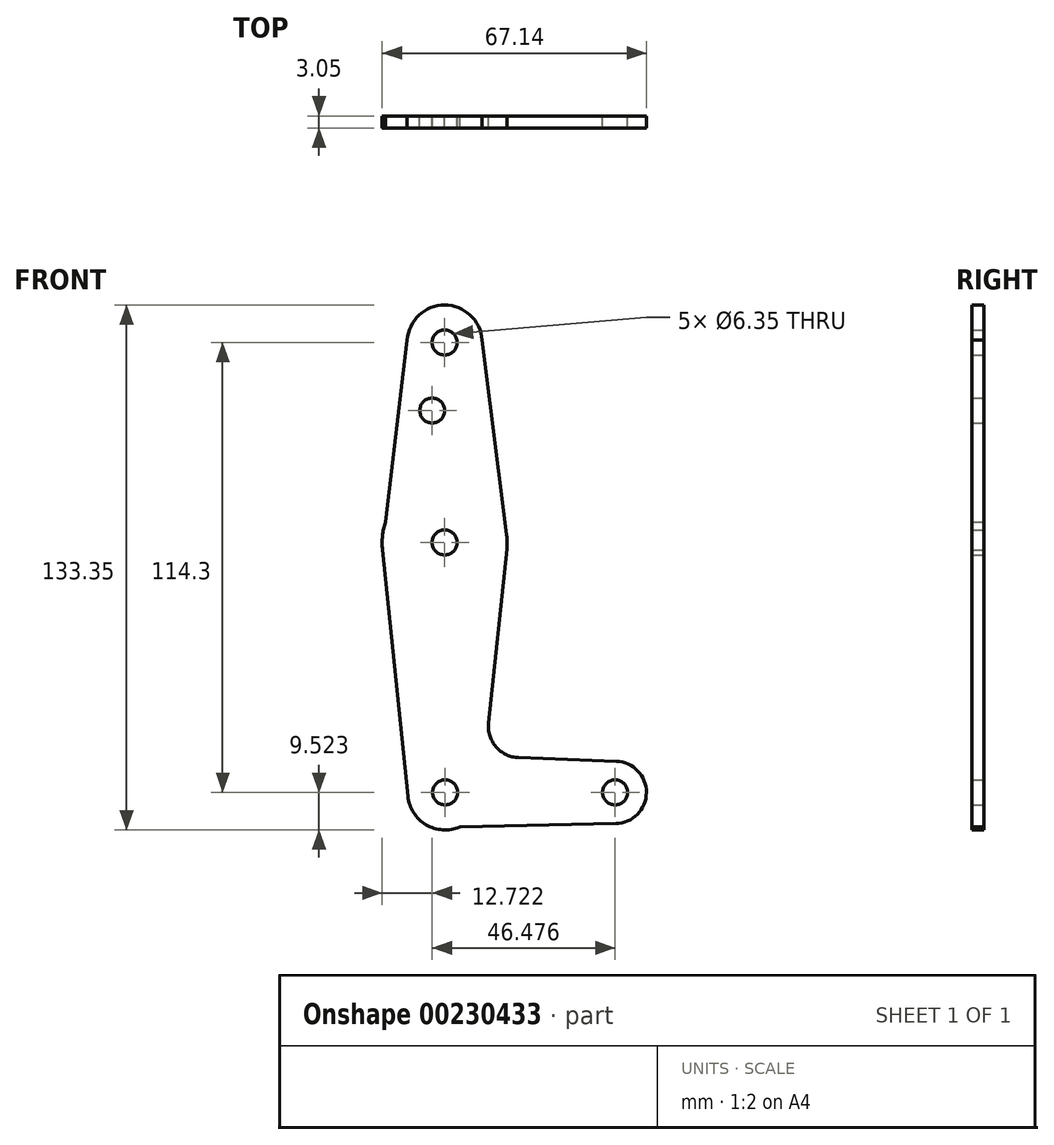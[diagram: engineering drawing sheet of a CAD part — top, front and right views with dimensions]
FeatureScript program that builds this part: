
annotation { "Feature Type Name" : "Feature", "Feature Type Description" : "" }
export const myFeature = defineFeature(function(context is Context, id is Id, definition is map)
    precondition{}
    {
        {
            var Q0;
            Q0=qCreatedBy(makeId("Front.planeOp"),FACE);
            var sketch = newSketch(context, id + "F0", { "sketchPlane" : qUnion([Q0])});
            skLineSegment(sketch, "E0", {"start": v(-35.23, -15.74) * mm, "end": v(7.95, -15.74) * mm});
            skCircle(sketch, "E1", {"center": v(-35.37, 98.56) * mm, "radius": 9.53 * mm});
            skCircle(sketch, "E2", {"center": v(-35.37, 47.76) * mm, "radius": 15.88 * mm});
            skCircle(sketch, "E3", {"center": v(-35.23, -15.74) * mm, "radius": 9.53 * mm});
            skCircle(sketch, "E4", {"center": v(7.95, -15.74) * mm, "radius": 7.94 * mm});
            skLineSegment(sketch, "E5", {"start": v(-35.37, 98.56) * mm, "end": v(-35.23, -15.74) * mm});
            skLineSegment(sketch, "E6", {"start": v(-44.88, 99.17) * mm, "end": v(-50.4, 52.9) * mm});
            skLineSegment(sketch, "E7", {"start": v(-25.87, 99.2) * mm, "end": v(-19.62, 49.75) * mm});
            skLineSegment(sketch, "E8", {"start": v(-19.59, 46.1) * mm, "end": v(-24.22, 1.88) * mm});
            skLineSegment(sketch, "E9", {"start": v(-51.2, 46.42) * mm, "end": v(-44.7, -16.71) * mm});
            skLineSegment(sketch, "E10", {"start": v(-38.57, -24.66) * mm, "end": v(8.12, -23.67) * mm});
            skLineSegment(sketch, "E11", {"start": v(-16.6, -6.9) * mm, "end": v(8.24, -7.8) * mm});
            skCircle(sketch, "E12", {"center": v(-35.37, 98.56) * mm, "radius": 3.18 * mm});
            skCircle(sketch, "E13", {"center": v(-38.53, 81.29) * mm, "radius": 3.18 * mm});
            skCircle(sketch, "E14", {"center": v(-35.37, 47.76) * mm, "radius": 3.18 * mm});
            skCircle(sketch, "E15", {"center": v(-35.23, -15.74) * mm, "radius": 3.18 * mm});
            skCircle(sketch, "E16", {"center": v(7.95, -15.74) * mm, "radius": 3.18 * mm});
            skArc(sketch, "E17.filletArc", {"start": v(-24.22, 1.88) * mm, "mid": v(-22.32, -4.16) * mm, "end": v(-16.6, -6.9) * mm});
            skSolve(sketch);
        }
        {
            var Q0;
            Q0 = qSketchRegion(id + "F0", true);
            extrude(context, id + "F1", {"entities" : qUnion([Q0]), "depth" : 3.05 * mm});
        }
        {
            var Q0;
            {var subQ0=sQuery(id+"F0.wireOp",EDGE,"E15");var subQ1=sQuery(id+"F0.wireOp",EDGE,"E0");var subQ2=makeQuery(id+"F0.imprint","INTERSECT",VERTEX,{"derivedFrom":[subQ1,subQ0]});Q0=makeQuery(id+"F0.imprint","IMPRINT",FACE,{"disambiguationData":[TD([[makeQuery(id+"F0.imprint","IMPRINT",EDGE,{"disambiguationData":[TD([[subQ2,-1.0]])],"derivedFrom":subQ1}),1.0]])]});}
            extrude(context, id + "F2", {"entities" : qUnion([Q0]), "operationType" : NewBodyOperationType.ADD, "depth" : 3.05 * mm});
        }
    });
